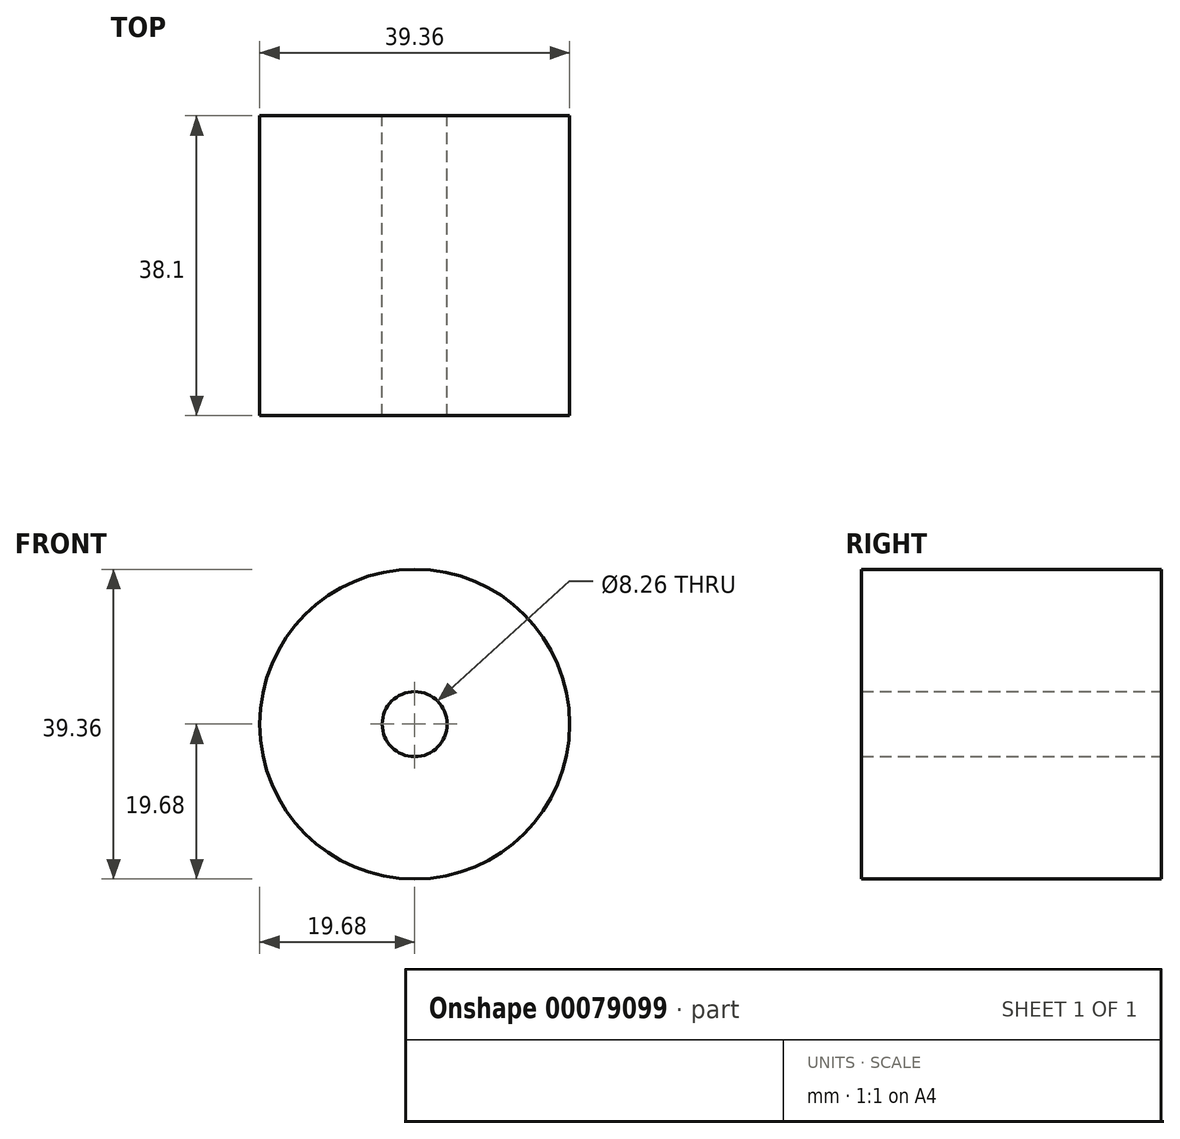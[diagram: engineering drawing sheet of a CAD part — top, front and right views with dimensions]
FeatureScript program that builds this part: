
annotation { "Feature Type Name" : "Feature", "Feature Type Description" : "" }
export const myFeature = defineFeature(function(context is Context, id is Id, definition is map)
    precondition{}
    {
        {
            var Q0;
            Q0=qCreatedBy(makeId("Front.planeOp"),FACE);
            var sketch = newSketch(context, id + "F0", { "sketchPlane" : qUnion([Q0])});
            skCircle(sketch, "E0", {"center": v(0, 0) * mm, "radius": 19.68 * mm});
            skCircle(sketch, "E1", {"center": v(0, 0) * mm, "radius": 4.13 * mm});
            skSolve(sketch);
        }
        {
            var Q0;
            Q0=makeQuery(id+"F0.imprint","IMPRINT",FACE,{"disambiguationData":[TD([[makeQuery(id+"F0.imprint","IMPRINT",EDGE,{"derivedFrom":sQuery(id+"F0.wireOp",EDGE,"E0")}),1.0]])]});
            extrude(context, id + "F1", {"entities" : qUnion([Q0]), "depth" : 38.1 * mm});
        }
    });
